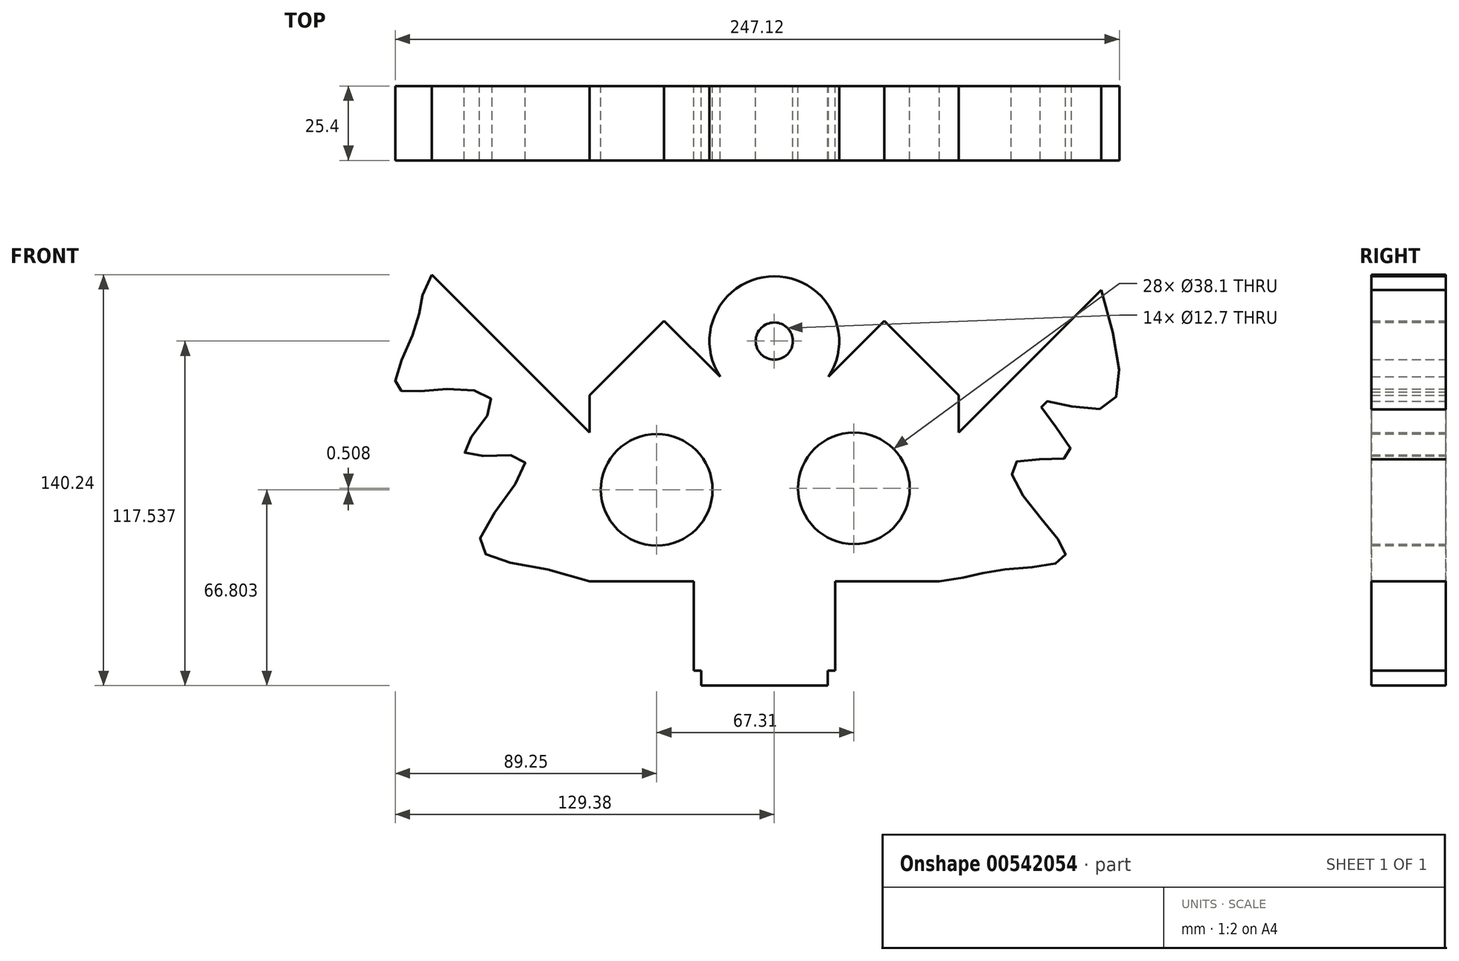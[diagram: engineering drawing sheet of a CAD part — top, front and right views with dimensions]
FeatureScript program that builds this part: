
annotation { "Feature Type Name" : "Feature", "Feature Type Description" : "" }
export const myFeature = defineFeature(function(context is Context, id is Id, definition is map)
    precondition{}
    {
        {
            var Q0;
            Q0=qCreatedBy(makeId("Front.planeOp"),FACE);
            var sketch = newSketch(context, id + "F0", { "sketchPlane" : qUnion([Q0])});
            skLineSegment(sketch, "E0", {"start": v(-18.44, -19.29) * mm, "end": v(-18.44, -49.77) * mm});
            skLineSegment(sketch, "E1", {"start": v(-18.44, -49.77) * mm, "end": v(-15.9, -49.77) * mm});
            skLineSegment(sketch, "E2", {"start": v(29.82, -19.29) * mm, "end": v(29.82, -49.77) * mm});
            skLineSegment(sketch, "E3", {"start": v(29.82, -49.77) * mm, "end": v(27.28, -49.77) * mm});
            skLineSegment(sketch, "E4", {"start": v(-15.9, -49.77) * mm, "end": v(-15.9, -54.85) * mm});
            skLineSegment(sketch, "E5", {"start": v(27.28, -49.77) * mm, "end": v(27.28, -54.85) * mm});
            skLineSegment(sketch, "E6", {"start": v(-15.9, -54.85) * mm, "end": v(27.28, -54.85) * mm});
            skLineSegment(sketch, "E7", {"start": v(-18.44, -19.29) * mm, "end": v(-54, -19.29) * mm});
            skLineSegment(sketch, "E8", {"start": v(29.82, -19.29) * mm, "end": v(65.38, -19.29) * mm});
            skLineSegment(sketch, "E9", {"start": v(-107.88, 85.4) * mm, "end": v(-54, 31.51) * mm});
            skLineSegment(sketch, "E10", {"start": v(71.98, 31.51) * mm, "end": v(125.86, 85.4) * mm});
            skFitSpline(sketch, "E11", {"points": [v(-107.88, 85.4) * mm, v(-113.33, 67.92) * mm, v(-120.15, 47.16) * mm, v(-104.34, 46.23) * mm, v(-87.3, 41.27) * mm, v(-96.6, 24.53) * mm, v(-76.45, 22.36) * mm, v(-91.63, -5.84) * mm, v(-54, -19.29) * mm], "startDerivative": vector(-117.26, -187.26) * mm, "endDerivative": vector(334.54, -128.82) * mm});
            skFitSpline(sketch, "E12", {"points": [v(65.38, -19.29) * mm, v(85.95, -15.44) * mm, v(107.96, -11.42) * mm, v(97.75, 4.86) * mm, v(91.35, 21.42) * mm, v(110.3, 24.18) * mm, v(99.8, 41.51) * mm, v(121.7, 39.9) * mm, v(119.3, 84.62) * mm], "startDerivative": vector(220, 20.33) * mm, "endDerivative": vector(-100.47, 344.12) * mm});
            skLineSegment(sketch, "E13", {"start": v(-54, 31.51) * mm, "end": v(-54, 44.21) * mm});
            skLineSegment(sketch, "E14", {"start": v(71.98, 31.51) * mm, "end": v(71.98, 44.21) * mm});
            skLineSegment(sketch, "E15", {"start": v(-54, 44.21) * mm, "end": v(-28.6, 69.61) * mm});
            skLineSegment(sketch, "E16", {"start": v(71.98, 44.21) * mm, "end": v(46.58, 69.61) * mm});
            skLineSegment(sketch, "E17", {"start": v(-28.6, 69.61) * mm, "end": v(-3.2, 44.21) * mm});
            skLineSegment(sketch, "E18", {"start": v(21.18, 44.21) * mm, "end": v(46.58, 69.61) * mm});
            skArc(sketch, "E19", {"start": v(21.18, 44.21) * mm, "mid": v(9, 84.82) * mm, "end": v(-3.2, 44.21) * mm});
            skCircle(sketch, "E20", {"center": v(9, 62.69) * mm, "radius": 6.35 * mm});
            skLineSegment(sketch, "E21", {"start": v(-18.44, -19.29) * mm, "end": v(-31.14, -19.29) * mm});
            skLineSegment(sketch, "E22", {"start": v(29.82, -19.29) * mm, "end": v(36.17, -19.29) * mm});
            skCircle(sketch, "E23", {"center": v(-31.14, 11.95) * mm, "radius": 19.05 * mm});
            skCircle(sketch, "E24", {"center": v(36.17, 12.46) * mm, "radius": 19.05 * mm});
            skSolve(sketch);
        }
        {
            var Q0;
            Q0 = qSketchRegion(id + "F0", true);
            extrude(context, id + "F1", {"entities" : qUnion([Q0]), "depth" : 25.4 * mm, "offsetDistance" : 25.4 * mm});
        }
    });
